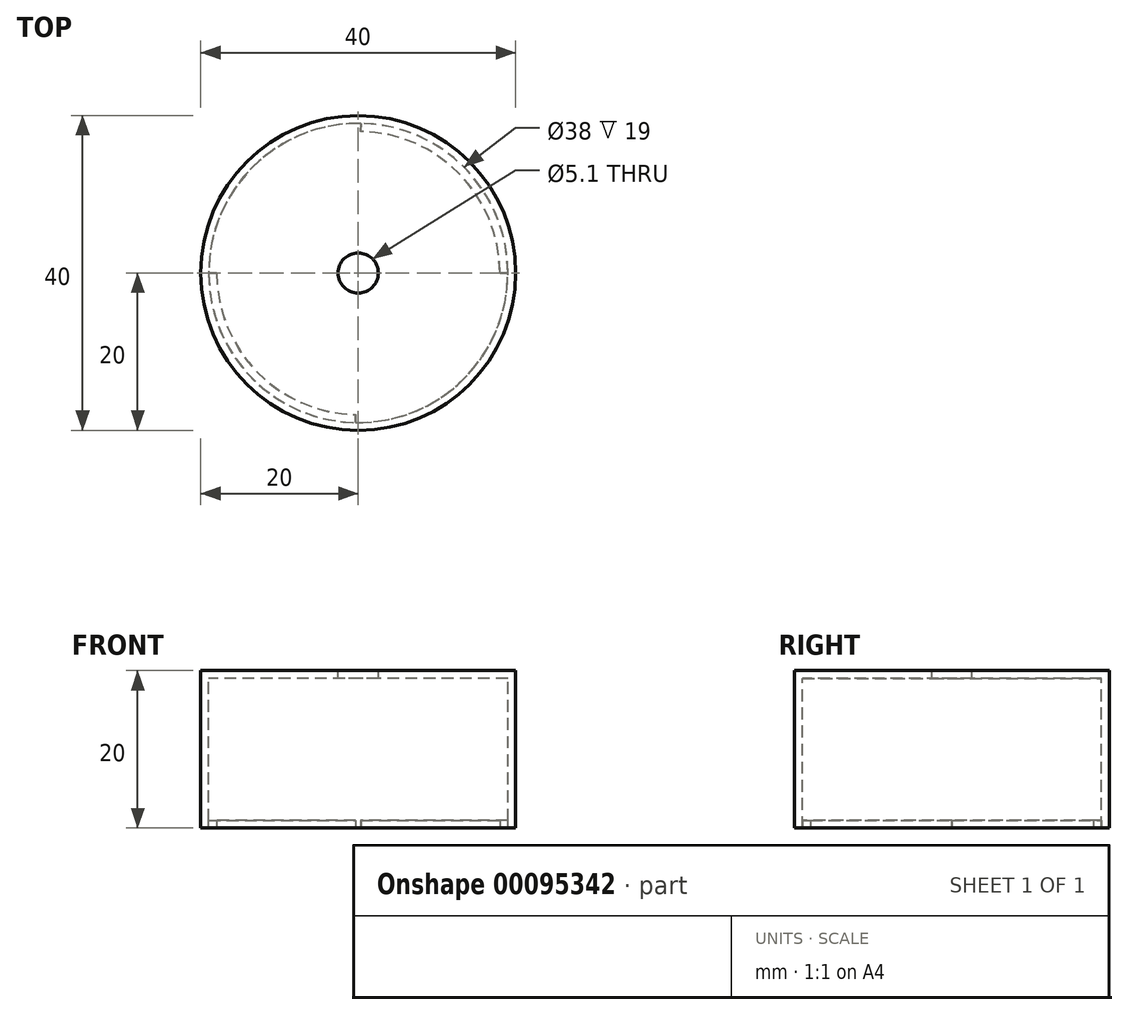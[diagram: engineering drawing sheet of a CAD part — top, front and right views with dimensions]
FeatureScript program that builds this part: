
annotation { "Feature Type Name" : "Feature", "Feature Type Description" : "" }
export const myFeature = defineFeature(function(context is Context, id is Id, definition is map)
    precondition{}
    {
        {
            var Q0;
            Q0=qCreatedBy(makeId("Front.planeOp"),FACE);
            var sketch = newSketch(context, id + "F0", { "sketchPlane" : qUnion([Q0])});
            skLineSegment(sketch, "E0", {"start": v(-20, 0) * mm, "end": v(-20, 20) * mm});
            skLineSegment(sketch, "E1", {"start": v(-20, 20) * mm, "end": v(0, 20) * mm});
            skLineSegment(sketch, "E2", {"start": v(0, 20) * mm, "end": v(0, 19) * mm});
            skLineSegment(sketch, "E3", {"start": v(0, 19) * mm, "end": v(-19, 19) * mm});
            skLineSegment(sketch, "E4", {"start": v(-19, 19) * mm, "end": v(-19, 1) * mm});
            skLineSegment(sketch, "E5", {"start": v(-19, 0) * mm, "end": v(-20, 0) * mm});
            skPoint(sketch, "E6", {"position": v(-20, 4.27) * mm});
            skPoint(sketch, "E7", {"position": v(-19, 4.44) * mm});
            skLineSegment(sketch, "E8", {"start": v(-19, 0) * mm, "end": v(-19, 1) * mm});
            skPoint(sketch, "E9.end.orphan", {"position": v(-18, 0) * mm});
            skPoint(sketch, "E10.end.orphan", {"position": v(-18, 1) * mm});
            skSolve(sketch);
        }
        {
            var Q0;
            Q0=makeQuery(id+"F0.imprint","IMPRINT",FACE,{"disambiguationData":[TD([[makeQuery(id+"F0.imprint","IMPRINT",EDGE,{"derivedFrom":sQuery(id+"F0.wireOp",EDGE,"E0")}),-1.0]])]});
            var Q1;
            Q1=sQuery(id+"F0.wireOp",EDGE,"E2");
            revolve(context, id + "F1", {"entities" : qUnion([Q0]), "axis" : qUnion([Q1]), "revolveType" : RevolveType.FULL});
        }
        {
            var Q0;
            Q0=makeQuery(id+"F1.opRevolve","SWEPT_FACE",FACE,{"disambiguationData":[OSD([sQuery(id+"F0.wireOp",EDGE,"E1")])]});
            var sketch = newSketch(context, id + "F2", { "sketchPlane" : qUnion([Q0])});
            skCircle(sketch, "E11", {"center": v(0, 0) * mm, "radius": 1.79 * mm});
            skSolve(sketch);
        }
        {
            var Q0;
            {var subQ0=makeQuery(id+"F2.imprint","IMPRINT",EDGE,{"derivedFrom":sQuery(id+"F2.wireOp",EDGE,"E11")});Q0=makeQuery(id+"F2.imprint","IMPRINT",BODY,{"disambiguationData":[TD([[makeQuery(id+"F2.imprint","IMPRINT",FACE,{"disambiguationData":[TD([[subQ0,1.0]])]}),1.0]])]});}
            deleteBodies(context, id + "F3", {"entities" : qUnion([Q0])});
        }
        {
            var Q0;
            Q0=makeQuery(id+"F1.opRevolve","SWEPT_FACE",FACE,{"disambiguationData":[OSD([sQuery(id+"F0.wireOp",EDGE,"E1")])]});
            var sketch = newSketch(context, id + "F7", { "sketchPlane" : qUnion([Q0])});
            skCircle(sketch, "E12", {"center": v(0, 0) * mm, "radius": 2.55 * mm});
            skSolve(sketch);
        }
        {
            var Q0;
            Q0=makeQuery(id+"F7.imprint","IMPRINT",FACE,{"disambiguationData":[TD([[makeQuery(id+"F7.imprint","IMPRINT",EDGE,{"derivedFrom":sQuery(id+"F7.wireOp",EDGE,"E12")}),1.0]])]});
            extrude(context, id + "F4", {"entities" : qUnion([Q0]), "operationType" : NewBodyOperationType.REMOVE, "oppositeDirection" : true, "depth" : 25 * mm});
        }
        {
            var Q0;
            Q0=qCreatedBy(makeId("Front.planeOp"),FACE);
            var sketch = newSketch(context, id + "F5", { "sketchPlane" : qUnion([Q0])});
            skLineSegment(sketch, "E13", {"start": v(-17.98, 0) * mm, "end": v(-19, 0) * mm});
            skLineSegment(sketch, "E14", {"start": v(-19, 0) * mm, "end": v(-19, 0.95) * mm});
            skLineSegment(sketch, "E15", {"start": v(-19, 0.95) * mm, "end": v(-17.99, 0.95) * mm});
            skLineSegment(sketch, "E16", {"start": v(-17.99, 0.95) * mm, "end": v(-17.98, 0) * mm});
            skLineSegment(sketch, "E17", {"start": v(0, 0) * mm, "end": v(0, 5.91) * mm, "construction": true});
            skLineSegment(sketch, "E18.MirrorCS", {"start": v(19, 0) * mm, "end": v(19, 0.95) * mm});
            skLineSegment(sketch, "E19.MirrorCS", {"start": v(17.98, 0) * mm, "end": v(19, 0) * mm});
            skLineSegment(sketch, "E20.MirrorCS", {"start": v(17.99, 0.95) * mm, "end": v(17.98, 0) * mm});
            skLineSegment(sketch, "E21.MirrorCS", {"start": v(19, 0.95) * mm, "end": v(17.99, 0.95) * mm});
            skSolve(sketch);
        }
        {
            var Q0;
            Q0 = qSketchRegion(id + "F5", true);
            var Q1;
            Q1=sQuery(id+"F5.wireOp",EDGE,"E17");
            revolve(context, id + "F6", {"operationType" : NewBodyOperationType.ADD, "entities" : qUnion([Q0]), "axis" : qUnion([Q1]), "revolveType" : RevolveType.ONE_DIRECTION, "angle" : 89 * degree});
        }
    });
